# Revit family: R1850
name_source: partatom
category: Pipe Accessories
revit_build: Autodesk Revit 2018 (Build: 20170223_1515(x64)
units: mm (PartAtom-declared; Revit-internal decimal feet)

## family parameters
Always vertical = Yes
Cut with Voids When Loaded = No
Part Type = Normal
Round Connector Dimension = Use Diameter
Shared = No
Work Plane-Based = No

## types (9) — shared parameters
Description = VENT STACK FLASHING SLEEVE
Floor Drain Material = Paint - Sherwin Williams Paint - #952C2A - Bellwood Red
Manufacturer = MIFAB
URL = WWW.MIFAB.COM

## per-type parameters (varying)
| type | C | K | Model | Pipe Diameter | Pipe Radius | Top D | Total Height |
| R1851.5_D-1 1/2"_VENT STACK FLASHING SLEEVE | 0' - 6 1/2" | 0' - 3" | R1851.5 | 0' - 1 1/2" | 0' - 1" | 0' - 2 1/2" | 0' - 8" |
| R1852_D-2"_VENT STACK FLASHING SLEEVE | 0' - 6 1/2" | 0' - 3" | R1852 | 0' - 2" | 0' - 1" | 0' - 3" | 0' - 8" |
| R1853_D-3"_VENT STACK FLASHING SLEEVE | 0' - 8 1/2" | 0' - 3" | R1853 | 0' - 3" | 0' - 1 1/2" | 0' - 4 1/2" | 0' - 8" |
| R1854_D-4"_VENT STACK FLASHING SLEEVE | 0' - 8 1/2" | 0' - 3" | R1854 | 0' - 4" | 0' - 2" | 0' - 5 1/2" | 0' - 8 1/2" |
| R1855_D-5"_VENT STACK FLASHING SLEEVE | 0' - 9 1/2" | 0' - 2 1/2" | R1855 | 0' - 5" | 0' - 2 1/2" | 0' - 6 1/2" | 0' - 8 1/2" |
| R1856_D-6"_VENT STACK FLASHING SLEEVE | 0' - 10 1/2" | 0' - 3" | R1856 | 0' - 6" | 0' - 3" | 0' - 7 1/2" | 0' - 8" |
| R1858_D-8"_VENT STACK FLASHING SLEEVE | 1' - 4 1/2" | 0' - 3" | R1858 | 0' - 8" | 0' - 4" | 0' - 11 1/2" | 0' - 9" |
| R1850-10_D-10"_VENT STACK FLASHING SLEEVE | 1' - 4 1/2" | 0' - 3" | R1850-10 | 0' - 10" | 0' - 5" | 0' - 11 1/2" | 0' - 9" |
| R1850-12_D-12"_VENT STACK FLASHING SLEEVE | 1' - 6 1/2" | 0' - 3" | R1850-12 | 1' - 0" | 0' - 6" | 1' - 1 1/2" | 0' - 9" |

## geometry (parser evidence)
native form markers: Sweep x2
no freeform markers — native parametric forms only
